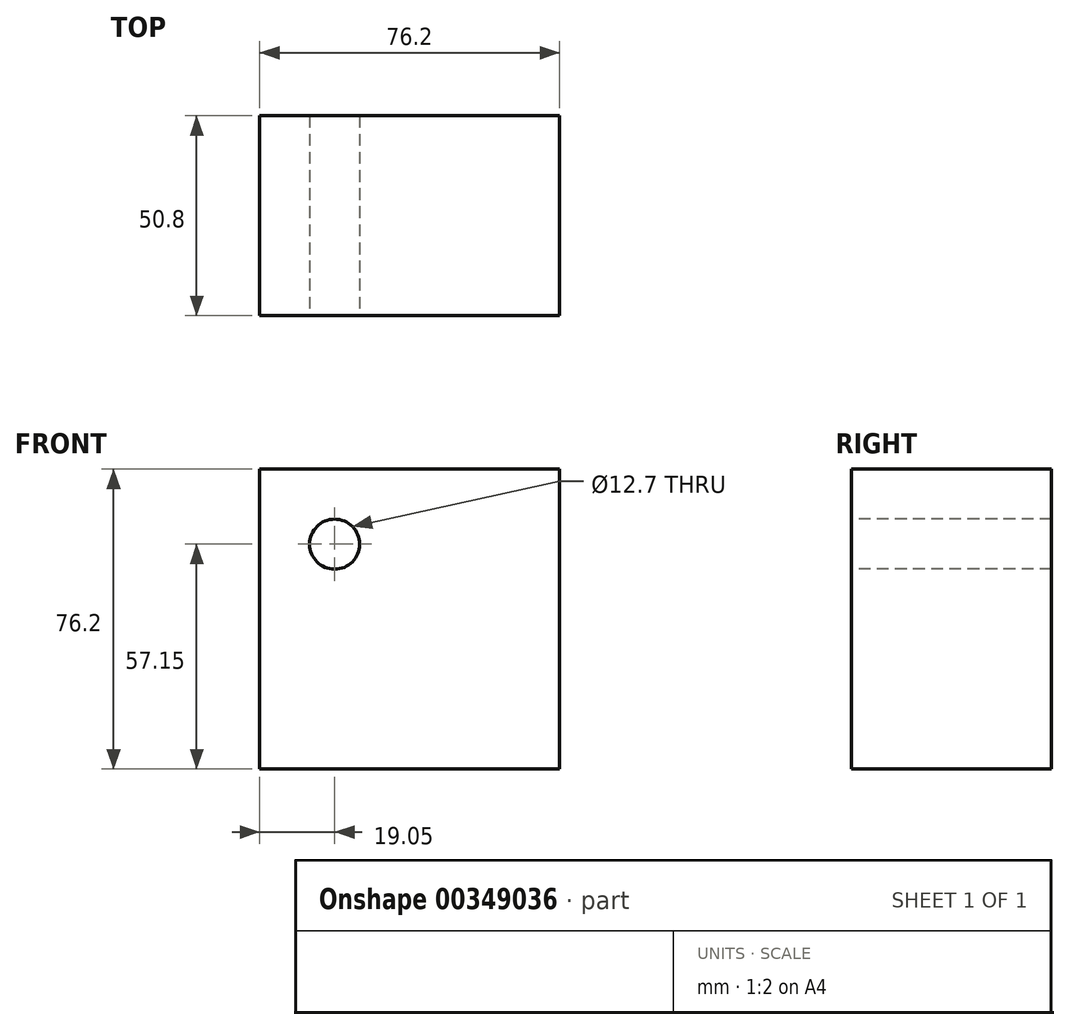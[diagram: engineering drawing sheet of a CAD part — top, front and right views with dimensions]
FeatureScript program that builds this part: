
annotation { "Feature Type Name" : "Feature", "Feature Type Description" : "" }
export const myFeature = defineFeature(function(context is Context, id is Id, definition is map)
    precondition{}
    {
        {
            var Q0;
            Q0=qCreatedBy(makeId("Front.planeOp"),FACE);
            var sketch = newSketch(context, id + "F0", { "sketchPlane" : qUnion([Q0])});
            skLineSegment(sketch, "E0.bottom", {"start": v(38.1, 38.1) * mm, "end": v(-38.1, 38.1) * mm});
            skLineSegment(sketch, "E0.top", {"start": v(38.1, -38.1) * mm, "end": v(-38.1, -38.1) * mm});
            skLineSegment(sketch, "E0.left", {"start": v(38.1, 38.1) * mm, "end": v(38.1, -38.1) * mm});
            skLineSegment(sketch, "E0.right", {"start": v(-38.1, 38.1) * mm, "end": v(-38.1, -38.1) * mm});
            skPoint(sketch, "E0.middle", {"position": v(0, 0) * mm});
            skSolve(sketch);
        }
        {
            var Q0;
            Q0=makeQuery(id+"F0.imprint","IMPRINT",FACE,{"disambiguationData":[TD([[makeQuery(id+"F0.imprint","IMPRINT",EDGE,{"derivedFrom":sQuery(id+"F0.wireOp",EDGE,"E0.bottom")}),1.0]])]});
            extrude(context, id + "F1", {"entities" : qUnion([Q0]), "endBound" : BoundingType.SYMMETRIC, "depth" : 50.8 * mm});
        }
        {
            var Q0;
            Q0=makeQuery(id+"F1.opExtrude","CAP_FACE",FACE,{"disambiguationData":[OSD([sQuery(id+"F0.wireOp",EDGE,"E0.bottom"),sQuery(id+"F0.wireOp",EDGE,"E0.top"),sQuery(id+"F0.wireOp",EDGE,"E0.left"),sQuery(id+"F0.wireOp",EDGE,"E0.right")])],"isStart":false});
            var sketch = newSketch(context, id + "F2", { "sketchPlane" : qUnion([Q0])});
            skCircle(sketch, "E1", {"center": v(-19.05, 19.05) * mm, "radius": 6.35 * mm});
            skSolve(sketch);
        }
        {
            var Q0;
            Q0=makeQuery(id+"F2.imprint","IMPRINT",FACE,{"disambiguationData":[TD([[makeQuery(id+"F2.imprint","IMPRINT",EDGE,{"derivedFrom":sQuery(id+"F2.wireOp",EDGE,"E1")}),1.0]])]});
            extrude(context, id + "F3", {"entities" : qUnion([Q0]), "operationType" : NewBodyOperationType.REMOVE, "endBound" : BoundingType.THROUGH_ALL, "oppositeDirection" : true, "depth" : 25.4 * mm});
        }
    });
